# Revit family: Шкафы шоковой заморозки
name_source: partatom
category: Оборудование
units: mm (PartAtom-declared; Revit-internal decimal feet)

## family parameters
Всегда вертикально = Да
Классификация = Нет
На основе рабочей плоскости = Нет
Общий = Нет
При загрузке вырезать с полостями = Нет
Размер круглого соединителя = Использовать диаметр
Тип детали = Нормальный
Точка расчета площади = Нет

## types (3) — shared parameters
IP 24 = +
Время замораживания = 240 минут
Время охлаждения = 90 минут
Замораживание от ... до ... темп. = +90 ... -18
Материал обшивок корпуса = нержавеющая сталь
Охлаждение от ... до ... темп. = +90 ... +3
Режим быстрого замораживания = +
Режим быстрого охлаждения = +
Режим мягкого замораживания = +
Режим мягкого охлаждения = +
Терморегулятор = электронный блок управления
Тип оттайки = автоматическая, горячим газом
Толщина стенки корпуса, мм = 61
Усл. окр. среды (тем., вл-сть %) = до +40
zero-valued in all types: Отметка по умолчанию

## per-type parameters (varying)
| type | Высокий | Габаритные размеры, мм | Кол-во уровней под GN1/1 или EN40/60 | Масса замораживаемого продукта, кг | Масса нетто/брутто, кг | Масса охлаждаемого продукта, кг | Низкий | Размеры в упаковке, мм | Система электропитания, В/Гц | Хладагент | Цена, руб. |
| GR5-G | Нет | 800х800х900 | 5 | 12 | 115/135 | 20 | Да | 920х1150х1000 | 230/50 | R404 | 155 500 |
| GR10-G | Да | 800х800х1670 | 10 | 25 | 175/210 | 35 | Нет | 920х1860х1000 | 230/50 | R404/R452 | 209 900 |
| GR10-G (380 W) | Да | 800х800х1670 | 10 | 25 | 175/210 | 35 | Нет | 920х1860х1000 | 400/50 | R404/R452 | 189 900 |
